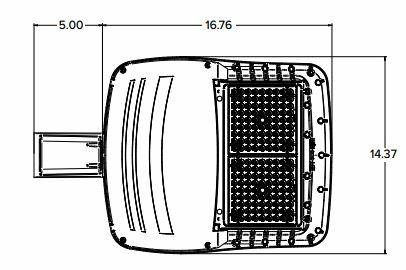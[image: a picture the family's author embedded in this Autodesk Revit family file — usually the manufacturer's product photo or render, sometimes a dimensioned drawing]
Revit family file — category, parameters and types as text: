
# Revit family: VP-1_AAU
name_source: partatom
category: Lighting Fixtures
units: mm (PartAtom-declared; Revit-internal decimal feet)

## family parameters
Cut with Voids When Loaded = No
Host = Face
Light Source = No
OmniClass Number = 23.80.70.11.14.17
OmniClass Title = Direct/Indirect
Part Type = Normal
Room Calculation Point = No
Round Connector Dimension = Use Diameter
Shared = Yes

## types (1)
- VP-1-AAU
    Apparent Load = 97 VA
    Assembly Code = D5020200
    Brand = Beacon
    CRI = 70
    Certification = UL
    Cool Grey = Cool Grey
    Default Elevation = 48 "
    Description = The Viper is an extremely versatile area/site luminaire which blends design, performance, and technology for a variety of applications.
    Features = Featuring two different optical technologies, Micro Strike and Strike Optics, which provide the best distribution patterns for retrofit or new construction
Vibration rated for high vibration applications including bridges and overpasses
Control options including photo control, occupancy sensing, NX Lighting Controls, wiSCAPE and 7-Pin with networked controls
Mounting options include: Arm, Universal Arm, Adjustable Arm, Mast Arm, Decorative Arm, Knuckle, Trunnion, Wall
Distribution options include: Auto Front Row, Type 2, Type 3, Type 4 Forward, Type 4 Wide, Type 5 Narrow, Type 5 Medium, Type 5 Wide, Type 5 Rectangular, Corner Optic, and Tennis Court
    Finish = Arctic White
    Glass = Glass
    Grey = Grey
    Lamp = LED
    Light Output = 6297 cd/m²
    Load Classification = Lighting
    Manufacturer = Current Lighting
    Matt Black = Matt Black
    Matt Grey = MATT GREY
    Matt White = Matt White
    Model = VP-1-AAU
    Name = Viper Area Size 1
    Power Factor = 0.9
    Product Documentation Link = https://cdn.currentlighting.com
    Product Page URL = https://www.currentlighting.com
    Type Comments = Lighting Fixture
    URL = https://www.currentlighting.com
    Voltage = 120 V
    Warranty = Five year warranty
    Wattage Comments = 97.2W

## geometry (parser evidence)
native form markers: Blend x2, Sweep x3
no freeform markers — native parametric forms only
